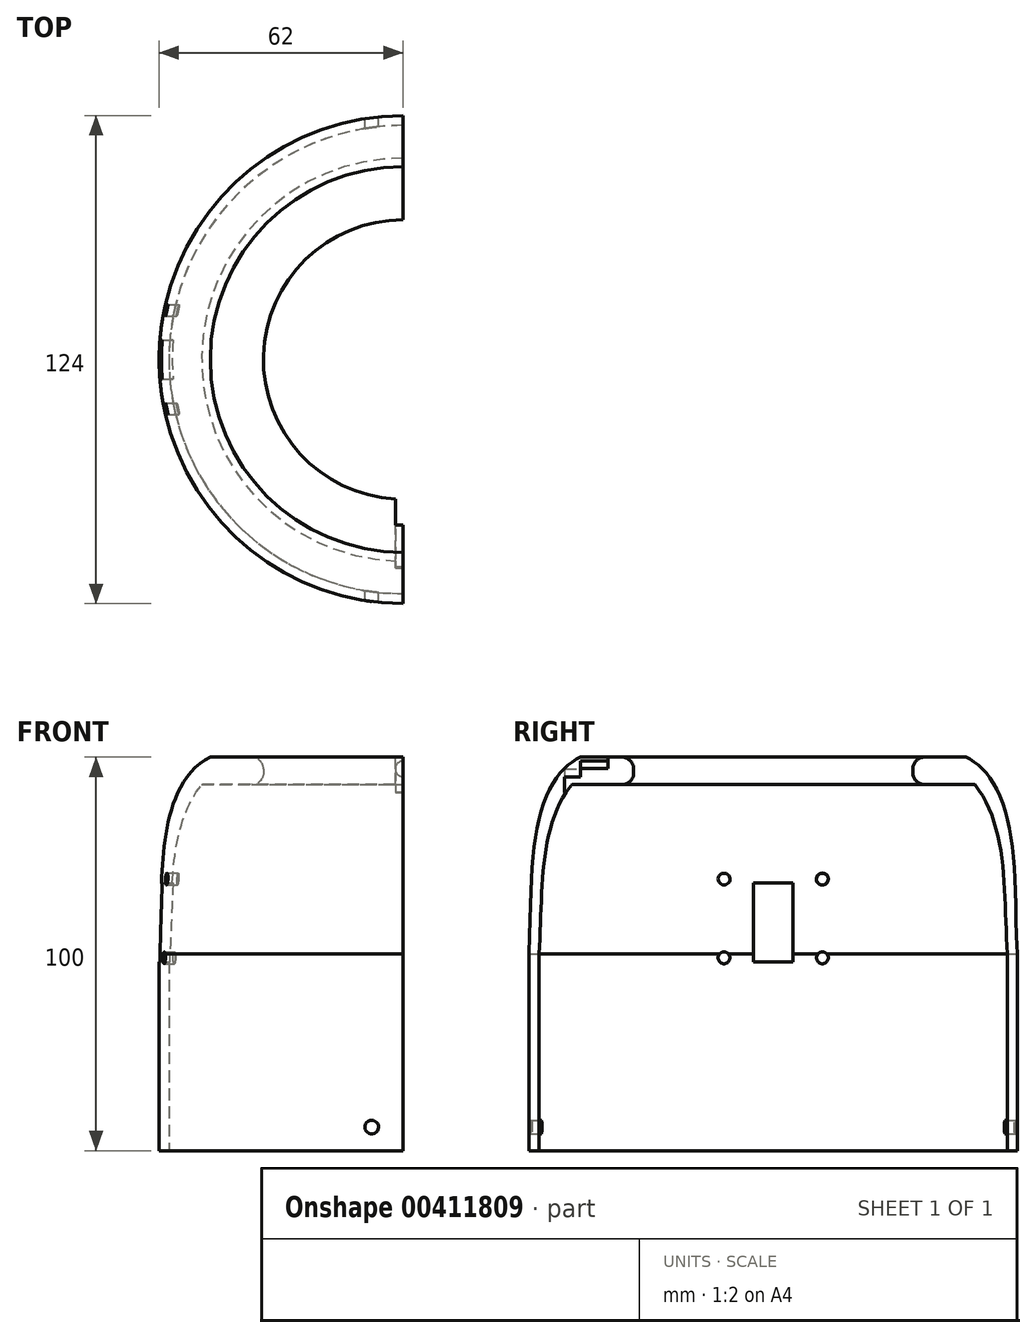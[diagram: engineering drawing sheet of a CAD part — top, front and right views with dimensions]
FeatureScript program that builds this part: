
annotation { "Feature Type Name" : "Feature", "Feature Type Description" : "" }
export const myFeature = defineFeature(function(context is Context, id is Id, definition is map)
    precondition{}
    {
        {
            var Q0;
            Q0=qCreatedBy(makeId("Front.planeOp"),FACE);
            var sketch = newSketch(context, id + "F0", { "sketchPlane" : qUnion([Q0])});
            skLineSegment(sketch, "E0", {"start": v(-38.5, 50) * mm, "end": v(-49, 50) * mm});
            skLineSegment(sketch, "E1", {"start": v(-62, 0) * mm, "end": v(-62, -50) * mm});
            skLineSegment(sketch, "E2", {"start": v(-35.5, 47) * mm, "end": v(-35.5, 46) * mm});
            skLineSegment(sketch, "E3", {"start": v(-38.5, 43) * mm, "end": v(-51.2, 43) * mm});
            skFitSpline(sketch, "E4", {"points": [v(-49, 50) * mm, v(-52.64, 47.47) * mm, v(-56.76, 41.98) * mm, v(-60.39, 29.9) * mm, v(-62, 0) * mm], "startDerivative": vector(-21.37, -10.6) * mm, "endDerivative": vector(-3.86, -109.3) * mm});
            skPoint(sketch, "E5.visualSharp", {"position": v(-35.5, 50) * mm});
            skArc(sketch, "E5.filletArc", {"start": v(-35.5, 47) * mm, "mid": v(-36.38, 49.12) * mm, "end": v(-38.5, 50) * mm});
            skPoint(sketch, "E6.visualSharp", {"position": v(-35.5, 43) * mm});
            skArc(sketch, "E6.filletArc", {"start": v(-38.5, 43) * mm, "mid": v(-36.38, 43.88) * mm, "end": v(-35.5, 46) * mm});
            skLineSegment(sketch, "E7", {"start": v(-62, -50) * mm, "end": v(0, -50) * mm});
            skLineSegment(sketch, "E8", {"start": v(-59.5, -50) * mm, "end": v(-59.5, 0) * mm});
            skFitSpline(sketch, "E9", {"points": [v(-51.2, 43) * mm, v(-59.5, 0) * mm], "startDerivative": vector(-25.81, -31.95) * mm, "endDerivative": vector(-3.04, -46.67) * mm});
            skLineSegment(sketch, "E10", {"start": v(0, -50) * mm, "end": v(0, -45.2) * mm});
            skSolve(sketch);
        }
        {
            var Q0;
            Q0=makeQuery(id+"F0.imprint","IMPRINT",FACE,{"disambiguationData":[TD([[makeQuery(id+"F0.imprint","IMPRINT",EDGE,{"derivedFrom":sQuery(id+"F0.wireOp",EDGE,"E0")}),1.0]])]});
            var Q1;
            Q1=sQuery(id+"F0.wireOp",EDGE,"E10");
            revolve(context, id + "F1", {"entities" : qUnion([Q0]), "axis" : qUnion([Q1]), "revolveType" : RevolveType.SYMMETRIC, "angle" : 180 * degree});
        }
        {
            var Q0;
            Q0=qCreatedBy(makeId("Front.planeOp"),FACE);
            var sketch = newSketch(context, id + "F2", { "sketchPlane" : qUnion([Q0])});
            skCircle(sketch, "E11", {"center": v(0, 47) * mm, "radius": 2 * mm});
            skLineSegment(sketch, "E12", {"start": v(-2, 47.07) * mm, "end": v(-2, 41.07) * mm});
            skLineSegment(sketch, "E13", {"start": v(-2, 41.07) * mm, "end": v(0, 41.07) * mm});
            skLineSegment(sketch, "E14", {"start": v(0, 41.07) * mm, "end": v(0, 45) * mm});
            skLineSegment(sketch, "E15", {"start": v(-2, 47.07) * mm, "end": v(-2, 50.36) * mm});
            skLineSegment(sketch, "E16", {"start": v(0, 50.36) * mm, "end": v(0, 49) * mm});
            skLineSegment(sketch, "E17", {"start": v(-2, 50.36) * mm, "end": v(0, 50.36) * mm});
            skSolve(sketch);
        }
        {
            var Q0;
            {var subQ1=sQuery(id+"F2.wireOp",EDGE,"E11");var subQ4=makeQuery(id+"F2.imprint","INTERSECT",VERTEX,{"derivedFrom":[subQ1,sQuery(id+"F2.wireOp",EDGE,"E14")]});Q0=makeQuery(id+"F2.imprint","IMPRINT",FACE,{"disambiguationData":[TD([[makeQuery(id+"F2.imprint","IMPRINT",EDGE,{"disambiguationData":[TD([[subQ4,1.0]])],"derivedFrom":subQ1}),1.0]])]});}
            extrude(context, id + "F3", {"entities" : qUnion([Q0]), "operationType" : NewBodyOperationType.REMOVE, "depth" : 49 * mm, "offsetDistance" : 25 * mm});
        }
        {
            var Q0;
            {var subQ0=sQuery(id+"F2.wireOp",EDGE,"E15");Q0=makeQuery(id+"F2.imprint","IMPRINT",FACE,{"disambiguationData":[TD([[makeQuery(id+"F2.imprint","IMPRINT",EDGE,{"derivedFrom":subQ0}),-1.0]])]});}
            extrude(context, id + "F4", {"entities" : qUnion([Q0]), "operationType" : NewBodyOperationType.REMOVE, "depth" : 42 * mm, "offsetDistance" : 25 * mm});
        }
        {
            var Q0;
            {var subQ4=sQuery(id+"F2.wireOp",EDGE,"E13");Q0=makeQuery(id+"F2.imprint","IMPRINT",FACE,{"disambiguationData":[TD([[makeQuery(id+"F2.imprint","IMPRINT",EDGE,{"derivedFrom":subQ4}),1.0]])]});}
            extrude(context, id + "F5", {"entities" : qUnion([Q0]), "operationType" : NewBodyOperationType.REMOVE, "depth" : 53 * mm, "offsetDistance" : 25 * mm});
        }
        {
            var Q0;
            Q0=qCreatedBy(makeId("Front.planeOp"),FACE);
            var sketch = newSketch(context, id + "F6", { "sketchPlane" : qUnion([Q0])});
            skCircle(sketch, "E18", {"center": v(-8, -44) * mm, "radius": 1.75 * mm});
            skSolve(sketch);
        }
        {
            var Q0;
            Q0=makeQuery(id+"F6.imprint","IMPRINT",FACE,{"disambiguationData":[TD([[makeQuery(id+"F6.imprint","IMPRINT",EDGE,{"derivedFrom":sQuery(id+"F6.wireOp",EDGE,"E18")}),1.0]])]});
            var Q1;
            Q1=sQuery(id+"F6.wireOp",EDGE,"E18");
            extrude(context, id + "F7", {"entities" : qUnion([Q0]), "operationType" : NewBodyOperationType.REMOVE, "surfaceEntities" : qUnion([Q1]), "depth" : 125 * mm, "symmetric" : true});
        }
        {
            var Q0;
            Q0=qCreatedBy(makeId("Right.planeOp"),FACE);
            var sketch = newSketch(context, id + "F8", { "sketchPlane" : qUnion([Q0])});
            skLineSegment(sketch, "E19.bottom", {"start": v(-5, 18) * mm, "end": v(5, 18) * mm});
            skLineSegment(sketch, "E19.top", {"start": v(-5, -2) * mm, "end": v(5, -2) * mm});
            skLineSegment(sketch, "E19.left", {"start": v(-5, 18) * mm, "end": v(-5, -2) * mm});
            skLineSegment(sketch, "E19.right", {"start": v(5, 18) * mm, "end": v(5, -2) * mm});
            skCircle(sketch, "E20", {"center": v(-12.5, 19) * mm, "radius": 1.5 * mm});
            skCircle(sketch, "E21.0.1.0", {"center": v(-12.5, -1) * mm, "radius": 1.5 * mm});
            skCircle(sketch, "E21.1.0.0", {"center": v(12.5, 19) * mm, "radius": 1.5 * mm});
            skCircle(sketch, "E21.1.1.0", {"center": v(12.5, -1) * mm, "radius": 1.5 * mm});
            skLineSegment(sketch, "E21.direction1", {"start": v(-12.5, 19) * mm, "end": v(12.5, 19) * mm, "construction": true});
            skLineSegment(sketch, "E21.direction2", {"start": v(-12.5, 19) * mm, "end": v(-12.5, -1) * mm, "construction": true});
            skSolve(sketch);
        }
        {
            var Q0;
            Q0=makeQuery(id+"F8.imprint","IMPRINT",FACE,{"disambiguationData":[TD([[makeQuery(id+"F8.imprint","IMPRINT",EDGE,{"derivedFrom":sQuery(id+"F8.wireOp",EDGE,"E19.bottom")}),-1.0]])]});
            var Q1;
            Q1=makeQuery(id+"F8.imprint","IMPRINT",FACE,{"disambiguationData":[TD([[makeQuery(id+"F8.imprint","IMPRINT",EDGE,{"derivedFrom":sQuery(id+"F8.wireOp",EDGE,"E20")}),1.0]])]});
            var Q2;
            Q2=makeQuery(id+"F8.imprint","IMPRINT",FACE,{"disambiguationData":[TD([[makeQuery(id+"F8.imprint","IMPRINT",EDGE,{"derivedFrom":sQuery(id+"F8.wireOp",EDGE,"E21.1.0.0")}),1.0]])]});
            var Q3;
            Q3=makeQuery(id+"F8.imprint","IMPRINT",FACE,{"disambiguationData":[TD([[makeQuery(id+"F8.imprint","IMPRINT",EDGE,{"derivedFrom":sQuery(id+"F8.wireOp",EDGE,"E21.1.1.0")}),1.0]])]});
            var Q4;
            Q4=makeQuery(id+"F8.imprint","IMPRINT",FACE,{"disambiguationData":[TD([[makeQuery(id+"F8.imprint","IMPRINT",EDGE,{"derivedFrom":sQuery(id+"F8.wireOp",EDGE,"E21.0.1.0")}),1.0]])]});
            extrude(context, id + "F9", {"entities" : qUnion([Q0, Q1, Q2, Q3, Q4]), "operationType" : NewBodyOperationType.REMOVE, "endBound" : BoundingType.THROUGH_ALL, "oppositeDirection" : true, "depth" : 25 * mm, "offsetDistance" : 25 * mm});
        }
    });
